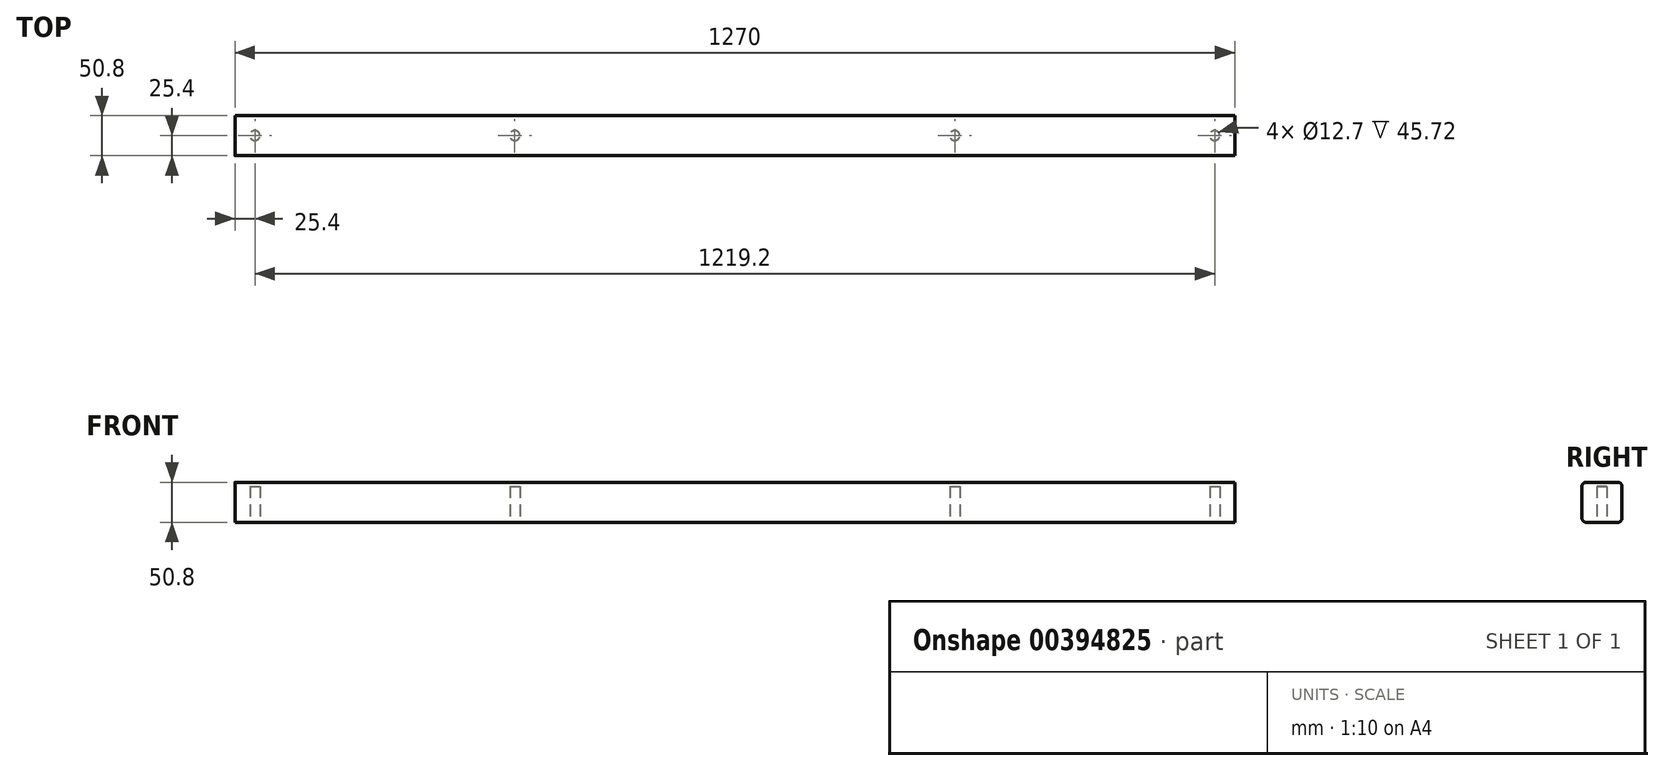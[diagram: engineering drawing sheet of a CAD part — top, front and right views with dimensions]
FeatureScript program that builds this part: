
annotation { "Feature Type Name" : "Feature", "Feature Type Description" : "" }
export const myFeature = defineFeature(function(context is Context, id is Id, definition is map)
    precondition{}
    {
        {
            var Q0;
            Q0=qCreatedBy(makeId("Front.planeOp"),FACE);
            var sketch = newSketch(context, id + "F0", { "sketchPlane" : qUnion([Q0])});
            skLineSegment(sketch, "E0", {"start": v(0, 216.73) * mm, "end": v(0, -403.5) * mm, "construction": true});
            skLineSegment(sketch, "E1", {"start": v(-169.2, 0) * mm, "end": v(472, 0) * mm, "construction": true});
            skLineSegment(sketch, "E2", {"start": v(0, 25.4) * mm, "end": v(635, 25.4) * mm});
            skLineSegment(sketch, "E3", {"start": v(635, 25.4) * mm, "end": v(635, 0) * mm});
            skLineSegment(sketch, "E4.MirrorCS", {"start": v(-635, 25.4) * mm, "end": v(-635, 0) * mm});
            skLineSegment(sketch, "E5.MirrorCS", {"start": v(0, 25.4) * mm, "end": v(-635, 25.4) * mm});
            skLineSegment(sketch, "E6.MirrorCS", {"start": v(-635, -25.4) * mm, "end": v(-635, 0) * mm});
            skLineSegment(sketch, "E7.MirrorCS", {"start": v(635, -25.4) * mm, "end": v(635, 0) * mm});
            skLineSegment(sketch, "E8.MirrorCS", {"start": v(0, -25.4) * mm, "end": v(-635, -25.4) * mm});
            skLineSegment(sketch, "E9.MirrorCS", {"start": v(0, -25.4) * mm, "end": v(635, -25.4) * mm});
            skSolve(sketch);
        }
        {
            var Q0;
            Q0=qSketchRegion(id+"F0",true);
            extrude(context, id + "F1", {"entities" : qUnion([Q0]), "depth" : 50.8 * mm});
        }
        {
            var Q0;
            Q0=makeQuery(id+"F1.opExtrude","CAP_EDGE",EDGE,{"disambiguationData":[OSD([sQuery(id+"F0.wireOp",EDGE,"E2"),sQuery(id+"F0.wireOp",EDGE,"E5.MirrorCS")])],"isStart":false});
            var Q1;
            Q1=makeQuery(id+"F1.opExtrude","CAP_EDGE",EDGE,{"disambiguationData":[OSD([sQuery(id+"F0.wireOp",EDGE,"E2"),sQuery(id+"F0.wireOp",EDGE,"E5.MirrorCS")])],"isStart":true});
            var Q2;
            Q2=makeQuery(id+"F1.opExtrude","CAP_EDGE",EDGE,{"disambiguationData":[OSD([sQuery(id+"F0.wireOp",EDGE,"E8.MirrorCS"),sQuery(id+"F0.wireOp",EDGE,"E9.MirrorCS")])],"isStart":false});
            var Q3;
            Q3=makeQuery(id+"F1.opExtrude","CAP_EDGE",EDGE,{"disambiguationData":[OSD([sQuery(id+"F0.wireOp",EDGE,"E8.MirrorCS"),sQuery(id+"F0.wireOp",EDGE,"E9.MirrorCS")])],"isStart":true});
            fillet(context, id + "F2", {"entities" : qUnion([Q0, Q1, Q2, Q3]), "radius" : 5.08 * mm, "tangentPropagation" : true, "allowEdgeOverflow" : false});
        }
        {
            var Q0;
            Q0=makeQuery(id+"F1.opExtrude","SWEPT_FACE",FACE,{"disambiguationData":[OSD([sQuery(id+"F0.wireOp",EDGE,"E8.MirrorCS"),sQuery(id+"F0.wireOp",EDGE,"E9.MirrorCS")])]});
            var sketch = newSketch(context, id + "F3", { "sketchPlane" : qUnion([Q0])});
            skPoint(sketch, "E10.0", {"position": v(0, 0) * mm});
            skLineSegment(sketch, "E11", {"start": v(0, 0) * mm, "end": v(0, 95.17) * mm, "construction": true});
            skPoint(sketch, "E12.0", {"position": v(635, 25.4) * mm});
            skLineSegment(sketch, "E13", {"start": v(635, 25.4) * mm, "end": v(0, 25.4) * mm, "construction": true});
            skCircle(sketch, "E14", {"center": v(279.4, 25.4) * mm, "radius": 6.35 * mm});
            skCircle(sketch, "E15", {"center": v(609.6, 25.4) * mm, "radius": 6.35 * mm});
            skCircle(sketch, "E16.MirrorC", {"center": v(-279.4, 25.4) * mm, "radius": 6.35 * mm});
            skCircle(sketch, "E17.MirrorC", {"center": v(-609.6, 25.4) * mm, "radius": 6.35 * mm});
            skSolve(sketch);
        }
        {
            var Q0;
            Q0=qSketchRegion(id+"F3",true);
            extrude(context, id + "F4", {"entities" : qUnion([Q0]), "operationType" : NewBodyOperationType.REMOVE, "oppositeDirection" : true, "depth" : 45.72 * mm});
        }
    });
